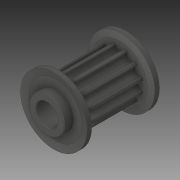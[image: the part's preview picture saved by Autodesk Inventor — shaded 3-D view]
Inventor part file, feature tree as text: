
AUTODESK INVENTOR PART (.ipt)
format: ipt  version: 2019 (Build 230136000, 136)  size: 216,064 bytes
history: native  units: in
note: dims shown in document units (in); Inventor stores cm internally (conversion verified against a paired STEP export)
features: chamfer x1
ambient origin geometry x8: Origin, YZ Plane, XZ Plane, XY Plane, X Axis, Y Axis, Z Axis, Center Point
bodies: Solid1 (feature_tree)
feature tree (1):
  chamfer  "Chamfer1"  [1 undecoded]
note: 1 required parameter value undecoded (feature->parameter linkage not recoverable at this tier; creation-order binding heuristic only, values carry confidence <= 0.55)
